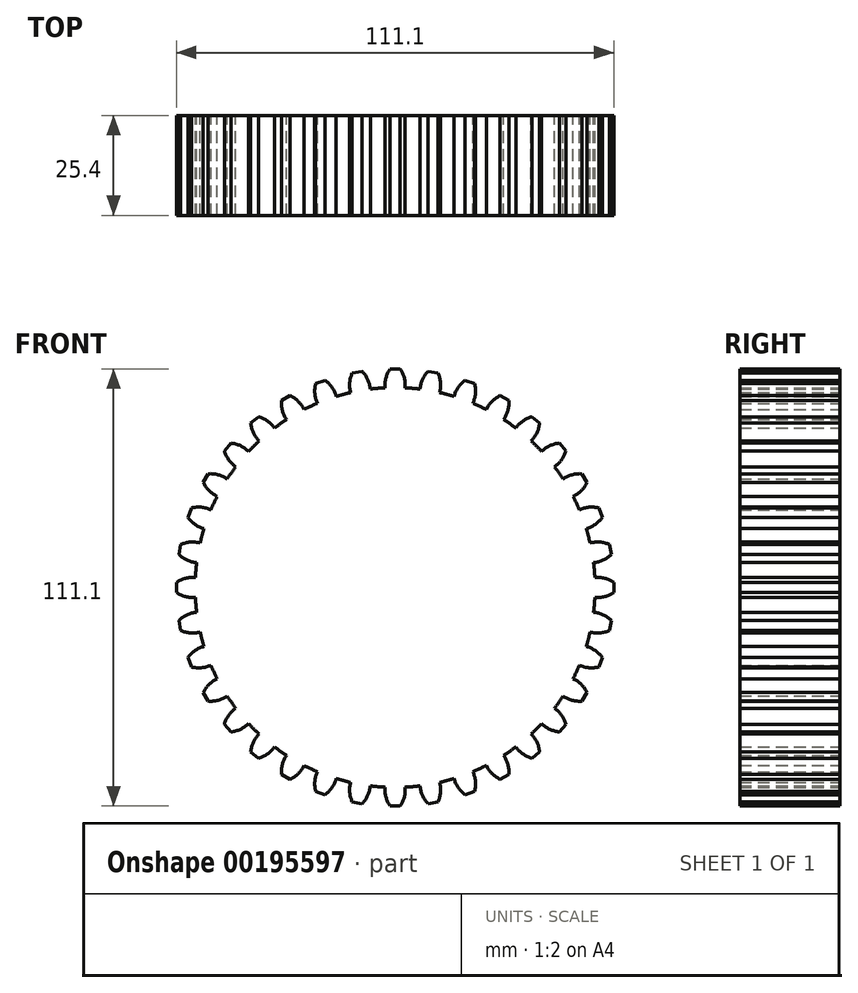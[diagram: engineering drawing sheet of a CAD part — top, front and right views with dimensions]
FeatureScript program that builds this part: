
annotation { "Feature Type Name" : "Feature", "Feature Type Description" : "" }
export const myFeature = defineFeature(function(context is Context, id is Id, definition is map)
    precondition{}
    {
        {
            var Q0;
            Q0=qCreatedBy(makeId("Front.planeOp"),FACE);
            var sketch = newSketch(context, id + "F0", { "sketchPlane" : qUnion([Q0])});
            skCircle(sketch, "E0", {"center": v(0, 0) * mm, "radius": 50.8 * mm});
            skPoint(sketch, "E1", {"position": v(0, 50.8) * mm});
            skPoint(sketch, "E2", {"position": v(0, 55.55) * mm});
            skPoint(sketch, "E3", {"position": v(-1.27, 55.55) * mm});
            skPoint(sketch, "E4", {"position": v(1.27, 55.55) * mm});
            skPoint(sketch, "E5", {"position": v(-2.54, 50.74) * mm});
            skPoint(sketch, "E6", {"position": v(2.54, 50.74) * mm});
            skArc(sketch, "E7", {"start": v(-1.27, 55.55) * mm, "mid": v(-2.32, 53.25) * mm, "end": v(-2.54, 50.74) * mm});
            skLineSegment(sketch, "E8", {"start": v(0, 55.55) * mm, "end": v(0, 50.8) * mm});
            skArc(sketch, "E9.MirrorCS", {"start": v(1.27, 55.55) * mm, "mid": v(2.32, 53.25) * mm, "end": v(2.54, 50.74) * mm});
            skLineSegment(sketch, "E10", {"start": v(-1.27, 55.55) * mm, "end": v(1.27, 55.55) * mm});
            skArc(sketch, "E11.1.0", {"start": v(-10.9, 54.49) * mm, "mid": v(-11.54, 52.04) * mm, "end": v(-11.31, 49.52) * mm});
            skLineSegment(sketch, "E11.1.1", {"start": v(-10.9, 54.49) * mm, "end": v(-8.4, 54.93) * mm});
            skArc(sketch, "E11.1.2", {"start": v(-8.4, 54.93) * mm, "mid": v(-6.96, 52.85) * mm, "end": v(-6.3, 50.4) * mm});
            skArc(sketch, "E11.2.0", {"start": v(-20.2, 51.77) * mm, "mid": v(-20.4, 49.25) * mm, "end": v(-19.74, 46.8) * mm});
            skLineSegment(sketch, "E11.2.1", {"start": v(-20.2, 51.77) * mm, "end": v(-17.8, 52.63) * mm});
            skArc(sketch, "E11.2.2", {"start": v(-17.8, 52.63) * mm, "mid": v(-16.03, 50.84) * mm, "end": v(-14.97, 48.55) * mm});
            skArc(sketch, "E11.3.0", {"start": v(-28.87, 47.47) * mm, "mid": v(-28.64, 44.96) * mm, "end": v(-27.57, 42.67) * mm});
            skLineSegment(sketch, "E11.3.1", {"start": v(-28.87, 47.47) * mm, "end": v(-26.68, 48.74) * mm});
            skArc(sketch, "E11.3.2", {"start": v(-26.68, 48.74) * mm, "mid": v(-24.61, 47.28) * mm, "end": v(-23.17, 45.2) * mm});
            skArc(sketch, "E11.4.0", {"start": v(-36.68, 41.74) * mm, "mid": v(-36.01, 39.3) * mm, "end": v(-34.56, 37.23) * mm});
            skLineSegment(sketch, "E11.4.1", {"start": v(-36.68, 41.74) * mm, "end": v(-34.73, 43.37) * mm});
            skArc(sketch, "E11.4.2", {"start": v(-34.73, 43.37) * mm, "mid": v(-32.45, 42.29) * mm, "end": v(-30.67, 40.5) * mm});
            skArc(sketch, "E11.5.0", {"start": v(-43.37, 34.73) * mm, "mid": v(-42.29, 32.45) * mm, "end": v(-40.5, 30.67) * mm});
            skLineSegment(sketch, "E11.5.1", {"start": v(-43.37, 34.73) * mm, "end": v(-41.74, 36.68) * mm});
            skArc(sketch, "E11.5.2", {"start": v(-41.74, 36.68) * mm, "mid": v(-39.3, 36.01) * mm, "end": v(-37.23, 34.56) * mm});
            skArc(sketch, "E11.6.0", {"start": v(-48.74, 26.68) * mm, "mid": v(-47.28, 24.61) * mm, "end": v(-45.2, 23.17) * mm});
            skLineSegment(sketch, "E11.6.1", {"start": v(-48.74, 26.68) * mm, "end": v(-47.47, 28.87) * mm});
            skArc(sketch, "E11.6.2", {"start": v(-47.47, 28.87) * mm, "mid": v(-44.96, 28.64) * mm, "end": v(-42.67, 27.57) * mm});
            skArc(sketch, "E11.7.0", {"start": v(-52.63, 17.8) * mm, "mid": v(-50.84, 16.03) * mm, "end": v(-48.55, 14.97) * mm});
            skLineSegment(sketch, "E11.7.1", {"start": v(-52.63, 17.8) * mm, "end": v(-51.77, 20.2) * mm});
            skArc(sketch, "E11.7.2", {"start": v(-51.77, 20.2) * mm, "mid": v(-49.25, 20.4) * mm, "end": v(-46.8, 19.74) * mm});
            skArc(sketch, "E11.8.0", {"start": v(-54.93, 8.4) * mm, "mid": v(-52.85, 6.96) * mm, "end": v(-50.4, 6.3) * mm});
            skLineSegment(sketch, "E11.8.1", {"start": v(-54.93, 8.4) * mm, "end": v(-54.49, 10.9) * mm});
            skArc(sketch, "E11.8.2", {"start": v(-54.49, 10.9) * mm, "mid": v(-52.04, 11.54) * mm, "end": v(-49.52, 11.31) * mm});
            skArc(sketch, "E11.9.0", {"start": v(-55.55, -1.27) * mm, "mid": v(-53.25, -2.32) * mm, "end": v(-50.74, -2.54) * mm});
            skLineSegment(sketch, "E11.9.1", {"start": v(-55.55, -1.27) * mm, "end": v(-55.55, 1.27) * mm});
            skArc(sketch, "E11.9.2", {"start": v(-55.55, 1.27) * mm, "mid": v(-53.25, 2.32) * mm, "end": v(-50.74, 2.54) * mm});
            skArc(sketch, "E11.10.0", {"start": v(-54.49, -10.9) * mm, "mid": v(-52.04, -11.54) * mm, "end": v(-49.52, -11.31) * mm});
            skLineSegment(sketch, "E11.10.1", {"start": v(-54.49, -10.9) * mm, "end": v(-54.93, -8.4) * mm});
            skArc(sketch, "E11.10.2", {"start": v(-54.93, -8.4) * mm, "mid": v(-52.85, -6.96) * mm, "end": v(-50.4, -6.3) * mm});
            skArc(sketch, "E11.11.0", {"start": v(-51.77, -20.2) * mm, "mid": v(-49.25, -20.4) * mm, "end": v(-46.8, -19.74) * mm});
            skLineSegment(sketch, "E11.11.1", {"start": v(-51.77, -20.2) * mm, "end": v(-52.63, -17.8) * mm});
            skArc(sketch, "E11.11.2", {"start": v(-52.63, -17.8) * mm, "mid": v(-50.84, -16.03) * mm, "end": v(-48.55, -14.97) * mm});
            skArc(sketch, "E11.12.0", {"start": v(-47.47, -28.87) * mm, "mid": v(-44.96, -28.64) * mm, "end": v(-42.67, -27.57) * mm});
            skLineSegment(sketch, "E11.12.1", {"start": v(-47.47, -28.87) * mm, "end": v(-48.74, -26.68) * mm});
            skArc(sketch, "E11.12.2", {"start": v(-48.74, -26.68) * mm, "mid": v(-47.28, -24.61) * mm, "end": v(-45.2, -23.17) * mm});
            skArc(sketch, "E11.13.0", {"start": v(-41.74, -36.68) * mm, "mid": v(-39.3, -36.01) * mm, "end": v(-37.23, -34.56) * mm});
            skLineSegment(sketch, "E11.13.1", {"start": v(-41.74, -36.68) * mm, "end": v(-43.37, -34.73) * mm});
            skArc(sketch, "E11.13.2", {"start": v(-43.37, -34.73) * mm, "mid": v(-42.29, -32.45) * mm, "end": v(-40.5, -30.67) * mm});
            skArc(sketch, "E11.14.0", {"start": v(-34.73, -43.37) * mm, "mid": v(-32.45, -42.29) * mm, "end": v(-30.67, -40.5) * mm});
            skLineSegment(sketch, "E11.14.1", {"start": v(-34.73, -43.37) * mm, "end": v(-36.68, -41.74) * mm});
            skArc(sketch, "E11.14.2", {"start": v(-36.68, -41.74) * mm, "mid": v(-36.01, -39.3) * mm, "end": v(-34.56, -37.23) * mm});
            skArc(sketch, "E11.15.0", {"start": v(-26.68, -48.74) * mm, "mid": v(-24.61, -47.28) * mm, "end": v(-23.17, -45.2) * mm});
            skLineSegment(sketch, "E11.15.1", {"start": v(-26.68, -48.74) * mm, "end": v(-28.87, -47.47) * mm});
            skArc(sketch, "E11.15.2", {"start": v(-28.87, -47.47) * mm, "mid": v(-28.64, -44.96) * mm, "end": v(-27.57, -42.67) * mm});
            skArc(sketch, "E11.16.0", {"start": v(-17.8, -52.63) * mm, "mid": v(-16.03, -50.84) * mm, "end": v(-14.97, -48.55) * mm});
            skLineSegment(sketch, "E11.16.1", {"start": v(-17.8, -52.63) * mm, "end": v(-20.2, -51.77) * mm});
            skArc(sketch, "E11.16.2", {"start": v(-20.2, -51.77) * mm, "mid": v(-20.4, -49.25) * mm, "end": v(-19.74, -46.8) * mm});
            skArc(sketch, "E11.17.0", {"start": v(-8.4, -54.93) * mm, "mid": v(-6.96, -52.85) * mm, "end": v(-6.3, -50.4) * mm});
            skLineSegment(sketch, "E11.17.1", {"start": v(-8.4, -54.93) * mm, "end": v(-10.9, -54.49) * mm});
            skArc(sketch, "E11.17.2", {"start": v(-10.9, -54.49) * mm, "mid": v(-11.54, -52.04) * mm, "end": v(-11.31, -49.52) * mm});
            skArc(sketch, "E11.18.0", {"start": v(1.27, -55.55) * mm, "mid": v(2.32, -53.25) * mm, "end": v(2.54, -50.74) * mm});
            skLineSegment(sketch, "E11.18.1", {"start": v(1.27, -55.55) * mm, "end": v(-1.27, -55.55) * mm});
            skArc(sketch, "E11.18.2", {"start": v(-1.27, -55.55) * mm, "mid": v(-2.32, -53.25) * mm, "end": v(-2.54, -50.74) * mm});
            skArc(sketch, "E11.19.0", {"start": v(10.9, -54.49) * mm, "mid": v(11.54, -52.04) * mm, "end": v(11.31, -49.52) * mm});
            skLineSegment(sketch, "E11.19.1", {"start": v(10.9, -54.49) * mm, "end": v(8.4, -54.93) * mm});
            skArc(sketch, "E11.19.2", {"start": v(8.4, -54.93) * mm, "mid": v(6.96, -52.85) * mm, "end": v(6.3, -50.4) * mm});
            skArc(sketch, "E11.20.0", {"start": v(20.2, -51.77) * mm, "mid": v(20.4, -49.25) * mm, "end": v(19.74, -46.8) * mm});
            skLineSegment(sketch, "E11.20.1", {"start": v(20.2, -51.77) * mm, "end": v(17.8, -52.63) * mm});
            skArc(sketch, "E11.20.2", {"start": v(17.8, -52.63) * mm, "mid": v(16.03, -50.84) * mm, "end": v(14.97, -48.55) * mm});
            skArc(sketch, "E11.21.0", {"start": v(28.87, -47.47) * mm, "mid": v(28.64, -44.96) * mm, "end": v(27.57, -42.67) * mm});
            skLineSegment(sketch, "E11.21.1", {"start": v(28.87, -47.47) * mm, "end": v(26.68, -48.74) * mm});
            skArc(sketch, "E11.21.2", {"start": v(26.68, -48.74) * mm, "mid": v(24.61, -47.28) * mm, "end": v(23.17, -45.2) * mm});
            skArc(sketch, "E11.22.0", {"start": v(36.68, -41.74) * mm, "mid": v(36.01, -39.3) * mm, "end": v(34.56, -37.23) * mm});
            skLineSegment(sketch, "E11.22.1", {"start": v(36.68, -41.74) * mm, "end": v(34.73, -43.37) * mm});
            skArc(sketch, "E11.22.2", {"start": v(34.73, -43.37) * mm, "mid": v(32.45, -42.29) * mm, "end": v(30.67, -40.5) * mm});
            skArc(sketch, "E11.23.0", {"start": v(43.37, -34.73) * mm, "mid": v(42.29, -32.45) * mm, "end": v(40.5, -30.67) * mm});
            skLineSegment(sketch, "E11.23.1", {"start": v(43.37, -34.73) * mm, "end": v(41.74, -36.68) * mm});
            skArc(sketch, "E11.23.2", {"start": v(41.74, -36.68) * mm, "mid": v(39.3, -36.01) * mm, "end": v(37.23, -34.56) * mm});
            skArc(sketch, "E11.24.0", {"start": v(48.74, -26.68) * mm, "mid": v(47.28, -24.61) * mm, "end": v(45.2, -23.17) * mm});
            skLineSegment(sketch, "E11.24.1", {"start": v(48.74, -26.68) * mm, "end": v(47.47, -28.87) * mm});
            skArc(sketch, "E11.24.2", {"start": v(47.47, -28.87) * mm, "mid": v(44.96, -28.64) * mm, "end": v(42.67, -27.57) * mm});
            skArc(sketch, "E11.25.0", {"start": v(52.63, -17.8) * mm, "mid": v(50.84, -16.03) * mm, "end": v(48.55, -14.97) * mm});
            skLineSegment(sketch, "E11.25.1", {"start": v(52.63, -17.8) * mm, "end": v(51.77, -20.2) * mm});
            skArc(sketch, "E11.25.2", {"start": v(51.77, -20.2) * mm, "mid": v(49.25, -20.4) * mm, "end": v(46.8, -19.74) * mm});
            skArc(sketch, "E11.26.0", {"start": v(54.93, -8.4) * mm, "mid": v(52.85, -6.96) * mm, "end": v(50.4, -6.3) * mm});
            skLineSegment(sketch, "E11.26.1", {"start": v(54.93, -8.4) * mm, "end": v(54.49, -10.9) * mm});
            skArc(sketch, "E11.26.2", {"start": v(54.49, -10.9) * mm, "mid": v(52.04, -11.54) * mm, "end": v(49.52, -11.31) * mm});
            skArc(sketch, "E11.27.0", {"start": v(55.55, 1.27) * mm, "mid": v(53.25, 2.32) * mm, "end": v(50.74, 2.54) * mm});
            skLineSegment(sketch, "E11.27.1", {"start": v(55.55, 1.27) * mm, "end": v(55.55, -1.27) * mm});
            skArc(sketch, "E11.27.2", {"start": v(55.55, -1.27) * mm, "mid": v(53.25, -2.32) * mm, "end": v(50.74, -2.54) * mm});
            skArc(sketch, "E11.28.0", {"start": v(54.49, 10.9) * mm, "mid": v(52.04, 11.54) * mm, "end": v(49.52, 11.31) * mm});
            skLineSegment(sketch, "E11.28.1", {"start": v(54.49, 10.9) * mm, "end": v(54.93, 8.4) * mm});
            skArc(sketch, "E11.28.2", {"start": v(54.93, 8.4) * mm, "mid": v(52.85, 6.96) * mm, "end": v(50.4, 6.3) * mm});
            skArc(sketch, "E11.29.0", {"start": v(51.77, 20.2) * mm, "mid": v(49.25, 20.4) * mm, "end": v(46.8, 19.74) * mm});
            skLineSegment(sketch, "E11.29.1", {"start": v(51.77, 20.2) * mm, "end": v(52.63, 17.8) * mm});
            skArc(sketch, "E11.29.2", {"start": v(52.63, 17.8) * mm, "mid": v(50.84, 16.03) * mm, "end": v(48.55, 14.97) * mm});
            skArc(sketch, "E11.30.0", {"start": v(47.47, 28.87) * mm, "mid": v(44.96, 28.64) * mm, "end": v(42.67, 27.57) * mm});
            skLineSegment(sketch, "E11.30.1", {"start": v(47.47, 28.87) * mm, "end": v(48.74, 26.68) * mm});
            skArc(sketch, "E11.30.2", {"start": v(48.74, 26.68) * mm, "mid": v(47.28, 24.61) * mm, "end": v(45.2, 23.17) * mm});
            skArc(sketch, "E11.31.0", {"start": v(41.74, 36.68) * mm, "mid": v(39.3, 36.01) * mm, "end": v(37.23, 34.56) * mm});
            skLineSegment(sketch, "E11.31.1", {"start": v(41.74, 36.68) * mm, "end": v(43.37, 34.73) * mm});
            skArc(sketch, "E11.31.2", {"start": v(43.37, 34.73) * mm, "mid": v(42.29, 32.45) * mm, "end": v(40.5, 30.67) * mm});
            skArc(sketch, "E11.32.0", {"start": v(34.73, 43.37) * mm, "mid": v(32.45, 42.29) * mm, "end": v(30.67, 40.5) * mm});
            skLineSegment(sketch, "E11.32.1", {"start": v(34.73, 43.37) * mm, "end": v(36.68, 41.74) * mm});
            skArc(sketch, "E11.32.2", {"start": v(36.68, 41.74) * mm, "mid": v(36.01, 39.3) * mm, "end": v(34.56, 37.23) * mm});
            skArc(sketch, "E11.33.0", {"start": v(26.68, 48.74) * mm, "mid": v(24.61, 47.28) * mm, "end": v(23.17, 45.2) * mm});
            skLineSegment(sketch, "E11.33.1", {"start": v(26.68, 48.74) * mm, "end": v(28.87, 47.47) * mm});
            skArc(sketch, "E11.33.2", {"start": v(28.87, 47.47) * mm, "mid": v(28.64, 44.96) * mm, "end": v(27.57, 42.67) * mm});
            skArc(sketch, "E11.34.0", {"start": v(17.8, 52.63) * mm, "mid": v(16.03, 50.84) * mm, "end": v(14.97, 48.55) * mm});
            skLineSegment(sketch, "E11.34.1", {"start": v(17.8, 52.63) * mm, "end": v(20.2, 51.77) * mm});
            skArc(sketch, "E11.34.2", {"start": v(20.2, 51.77) * mm, "mid": v(20.4, 49.25) * mm, "end": v(19.74, 46.8) * mm});
            skArc(sketch, "E11.35.0", {"start": v(8.4, 54.93) * mm, "mid": v(6.96, 52.85) * mm, "end": v(6.3, 50.4) * mm});
            skLineSegment(sketch, "E11.35.1", {"start": v(8.4, 54.93) * mm, "end": v(10.9, 54.49) * mm});
            skArc(sketch, "E11.35.2", {"start": v(10.9, 54.49) * mm, "mid": v(11.54, 52.04) * mm, "end": v(11.31, 49.52) * mm});
            skSolve(sketch);
        }
        {
            var Q0;
            {var subQ0=sQuery(id+"F0.wireOp",EDGE,"E0");var subQ35=makeQuery(id+"F0.imprint","INTERSECT",VERTEX,{"derivedFrom":[subQ0,sQuery(id+"F0.wireOp",EDGE,"E11.27.0")]});Q0=makeQuery(id+"F0.imprint","IMPRINT",FACE,{"disambiguationData":[TD([[makeQuery(id+"F0.imprint","IMPRINT",EDGE,{"disambiguationData":[TD([[subQ35,-1.0]])],"derivedFrom":subQ0}),1.0]])]});}
            var Q1;
            {var subQ0=sQuery(id+"F0.wireOp",EDGE,"E11.6.0");Q1=makeQuery(id+"F0.imprint","IMPRINT",FACE,{"disambiguationData":[TD([[makeQuery(id+"F0.imprint","IMPRINT",EDGE,{"derivedFrom":subQ0}),1.0]])]});}
            var Q2;
            {var subQ0=sQuery(id+"F0.wireOp",EDGE,"E11.7.0");Q2=makeQuery(id+"F0.imprint","IMPRINT",FACE,{"disambiguationData":[TD([[makeQuery(id+"F0.imprint","IMPRINT",EDGE,{"derivedFrom":subQ0}),1.0]])]});}
            var Q3;
            {var subQ0=sQuery(id+"F0.wireOp",EDGE,"E11.8.0");Q3=makeQuery(id+"F0.imprint","IMPRINT",FACE,{"disambiguationData":[TD([[makeQuery(id+"F0.imprint","IMPRINT",EDGE,{"derivedFrom":subQ0}),1.0]])]});}
            var Q4;
            {var subQ0=sQuery(id+"F0.wireOp",EDGE,"E11.9.0");Q4=makeQuery(id+"F0.imprint","IMPRINT",FACE,{"disambiguationData":[TD([[makeQuery(id+"F0.imprint","IMPRINT",EDGE,{"derivedFrom":subQ0}),1.0]])]});}
            var Q5;
            {var subQ0=sQuery(id+"F0.wireOp",EDGE,"E11.10.0");Q5=makeQuery(id+"F0.imprint","IMPRINT",FACE,{"disambiguationData":[TD([[makeQuery(id+"F0.imprint","IMPRINT",EDGE,{"derivedFrom":subQ0}),1.0]])]});}
            var Q6;
            {var subQ0=sQuery(id+"F0.wireOp",EDGE,"E11.11.0");Q6=makeQuery(id+"F0.imprint","IMPRINT",FACE,{"disambiguationData":[TD([[makeQuery(id+"F0.imprint","IMPRINT",EDGE,{"derivedFrom":subQ0}),1.0]])]});}
            var Q7;
            {var subQ0=sQuery(id+"F0.wireOp",EDGE,"E11.12.0");Q7=makeQuery(id+"F0.imprint","IMPRINT",FACE,{"disambiguationData":[TD([[makeQuery(id+"F0.imprint","IMPRINT",EDGE,{"derivedFrom":subQ0}),1.0]])]});}
            var Q8;
            {var subQ0=sQuery(id+"F0.wireOp",EDGE,"E11.13.0");Q8=makeQuery(id+"F0.imprint","IMPRINT",FACE,{"disambiguationData":[TD([[makeQuery(id+"F0.imprint","IMPRINT",EDGE,{"derivedFrom":subQ0}),1.0]])]});}
            var Q9;
            {var subQ0=sQuery(id+"F0.wireOp",EDGE,"E11.14.0");Q9=makeQuery(id+"F0.imprint","IMPRINT",FACE,{"disambiguationData":[TD([[makeQuery(id+"F0.imprint","IMPRINT",EDGE,{"derivedFrom":subQ0}),1.0]])]});}
            var Q10;
            {var subQ0=sQuery(id+"F0.wireOp",EDGE,"E11.15.0");Q10=makeQuery(id+"F0.imprint","IMPRINT",FACE,{"disambiguationData":[TD([[makeQuery(id+"F0.imprint","IMPRINT",EDGE,{"derivedFrom":subQ0}),1.0]])]});}
            var Q11;
            {var subQ0=sQuery(id+"F0.wireOp",EDGE,"E11.16.0");Q11=makeQuery(id+"F0.imprint","IMPRINT",FACE,{"disambiguationData":[TD([[makeQuery(id+"F0.imprint","IMPRINT",EDGE,{"derivedFrom":subQ0}),1.0]])]});}
            var Q12;
            {var subQ0=sQuery(id+"F0.wireOp",EDGE,"E11.17.0");Q12=makeQuery(id+"F0.imprint","IMPRINT",FACE,{"disambiguationData":[TD([[makeQuery(id+"F0.imprint","IMPRINT",EDGE,{"derivedFrom":subQ0}),1.0]])]});}
            var Q13;
            {var subQ0=sQuery(id+"F0.wireOp",EDGE,"E11.18.0");Q13=makeQuery(id+"F0.imprint","IMPRINT",FACE,{"disambiguationData":[TD([[makeQuery(id+"F0.imprint","IMPRINT",EDGE,{"derivedFrom":subQ0}),1.0]])]});}
            var Q14;
            {var subQ0=sQuery(id+"F0.wireOp",EDGE,"E11.19.0");Q14=makeQuery(id+"F0.imprint","IMPRINT",FACE,{"disambiguationData":[TD([[makeQuery(id+"F0.imprint","IMPRINT",EDGE,{"derivedFrom":subQ0}),1.0]])]});}
            var Q15;
            {var subQ0=sQuery(id+"F0.wireOp",EDGE,"E11.20.0");Q15=makeQuery(id+"F0.imprint","IMPRINT",FACE,{"disambiguationData":[TD([[makeQuery(id+"F0.imprint","IMPRINT",EDGE,{"derivedFrom":subQ0}),1.0]])]});}
            var Q16;
            {var subQ0=sQuery(id+"F0.wireOp",EDGE,"E11.21.0");Q16=makeQuery(id+"F0.imprint","IMPRINT",FACE,{"disambiguationData":[TD([[makeQuery(id+"F0.imprint","IMPRINT",EDGE,{"derivedFrom":subQ0}),1.0]])]});}
            var Q17;
            {var subQ0=sQuery(id+"F0.wireOp",EDGE,"E11.22.0");Q17=makeQuery(id+"F0.imprint","IMPRINT",FACE,{"disambiguationData":[TD([[makeQuery(id+"F0.imprint","IMPRINT",EDGE,{"derivedFrom":subQ0}),1.0]])]});}
            var Q18;
            {var subQ0=sQuery(id+"F0.wireOp",EDGE,"E11.23.0");Q18=makeQuery(id+"F0.imprint","IMPRINT",FACE,{"disambiguationData":[TD([[makeQuery(id+"F0.imprint","IMPRINT",EDGE,{"derivedFrom":subQ0}),1.0]])]});}
            var Q19;
            {var subQ0=sQuery(id+"F0.wireOp",EDGE,"E11.24.0");Q19=makeQuery(id+"F0.imprint","IMPRINT",FACE,{"disambiguationData":[TD([[makeQuery(id+"F0.imprint","IMPRINT",EDGE,{"derivedFrom":subQ0}),1.0]])]});}
            var Q20;
            {var subQ0=sQuery(id+"F0.wireOp",EDGE,"E11.25.0");Q20=makeQuery(id+"F0.imprint","IMPRINT",FACE,{"disambiguationData":[TD([[makeQuery(id+"F0.imprint","IMPRINT",EDGE,{"derivedFrom":subQ0}),1.0]])]});}
            var Q21;
            {var subQ0=sQuery(id+"F0.wireOp",EDGE,"E11.26.0");Q21=makeQuery(id+"F0.imprint","IMPRINT",FACE,{"disambiguationData":[TD([[makeQuery(id+"F0.imprint","IMPRINT",EDGE,{"derivedFrom":subQ0}),1.0]])]});}
            var Q22;
            {var subQ0=sQuery(id+"F0.wireOp",EDGE,"E11.27.0");Q22=makeQuery(id+"F0.imprint","IMPRINT",FACE,{"disambiguationData":[TD([[makeQuery(id+"F0.imprint","IMPRINT",EDGE,{"derivedFrom":subQ0}),1.0]])]});}
            var Q23;
            {var subQ0=sQuery(id+"F0.wireOp",EDGE,"E11.28.0");Q23=makeQuery(id+"F0.imprint","IMPRINT",FACE,{"disambiguationData":[TD([[makeQuery(id+"F0.imprint","IMPRINT",EDGE,{"derivedFrom":subQ0}),1.0]])]});}
            var Q24;
            {var subQ0=sQuery(id+"F0.wireOp",EDGE,"E11.29.0");Q24=makeQuery(id+"F0.imprint","IMPRINT",FACE,{"disambiguationData":[TD([[makeQuery(id+"F0.imprint","IMPRINT",EDGE,{"derivedFrom":subQ0}),1.0]])]});}
            var Q25;
            {var subQ0=sQuery(id+"F0.wireOp",EDGE,"E11.30.0");Q25=makeQuery(id+"F0.imprint","IMPRINT",FACE,{"disambiguationData":[TD([[makeQuery(id+"F0.imprint","IMPRINT",EDGE,{"derivedFrom":subQ0}),1.0]])]});}
            var Q26;
            {var subQ0=sQuery(id+"F0.wireOp",EDGE,"E11.31.0");Q26=makeQuery(id+"F0.imprint","IMPRINT",FACE,{"disambiguationData":[TD([[makeQuery(id+"F0.imprint","IMPRINT",EDGE,{"derivedFrom":subQ0}),1.0]])]});}
            var Q27;
            {var subQ0=sQuery(id+"F0.wireOp",EDGE,"E11.32.0");Q27=makeQuery(id+"F0.imprint","IMPRINT",FACE,{"disambiguationData":[TD([[makeQuery(id+"F0.imprint","IMPRINT",EDGE,{"derivedFrom":subQ0}),1.0]])]});}
            var Q28;
            {var subQ0=sQuery(id+"F0.wireOp",EDGE,"E11.33.0");Q28=makeQuery(id+"F0.imprint","IMPRINT",FACE,{"disambiguationData":[TD([[makeQuery(id+"F0.imprint","IMPRINT",EDGE,{"derivedFrom":subQ0}),1.0]])]});}
            var Q29;
            {var subQ0=sQuery(id+"F0.wireOp",EDGE,"E11.34.0");Q29=makeQuery(id+"F0.imprint","IMPRINT",FACE,{"disambiguationData":[TD([[makeQuery(id+"F0.imprint","IMPRINT",EDGE,{"derivedFrom":subQ0}),1.0]])]});}
            var Q30;
            {var subQ0=sQuery(id+"F0.wireOp",EDGE,"E11.35.0");Q30=makeQuery(id+"F0.imprint","IMPRINT",FACE,{"disambiguationData":[TD([[makeQuery(id+"F0.imprint","IMPRINT",EDGE,{"derivedFrom":subQ0}),1.0]])]});}
            var Q31;
            {var subQ0=sQuery(id+"F0.wireOp",EDGE,"E7");Q31=makeQuery(id+"F0.imprint","IMPRINT",FACE,{"disambiguationData":[TD([[makeQuery(id+"F0.imprint","IMPRINT",EDGE,{"derivedFrom":subQ0}),1.0]])]});}
            var Q32;
            {var subQ0=sQuery(id+"F0.wireOp",EDGE,"E11.5.0");Q32=makeQuery(id+"F0.imprint","IMPRINT",FACE,{"disambiguationData":[TD([[makeQuery(id+"F0.imprint","IMPRINT",EDGE,{"derivedFrom":subQ0}),1.0]])]});}
            var Q33;
            {var subQ0=sQuery(id+"F0.wireOp",EDGE,"E11.4.0");Q33=makeQuery(id+"F0.imprint","IMPRINT",FACE,{"disambiguationData":[TD([[makeQuery(id+"F0.imprint","IMPRINT",EDGE,{"derivedFrom":subQ0}),1.0]])]});}
            var Q34;
            {var subQ0=sQuery(id+"F0.wireOp",EDGE,"E11.3.0");Q34=makeQuery(id+"F0.imprint","IMPRINT",FACE,{"disambiguationData":[TD([[makeQuery(id+"F0.imprint","IMPRINT",EDGE,{"derivedFrom":subQ0}),1.0]])]});}
            var Q35;
            {var subQ0=sQuery(id+"F0.wireOp",EDGE,"E11.2.0");Q35=makeQuery(id+"F0.imprint","IMPRINT",FACE,{"disambiguationData":[TD([[makeQuery(id+"F0.imprint","IMPRINT",EDGE,{"derivedFrom":subQ0}),1.0]])]});}
            var Q36;
            {var subQ0=sQuery(id+"F0.wireOp",EDGE,"E11.1.0");Q36=makeQuery(id+"F0.imprint","IMPRINT",FACE,{"disambiguationData":[TD([[makeQuery(id+"F0.imprint","IMPRINT",EDGE,{"derivedFrom":subQ0}),1.0]])]});}
            var Q37;
            {var subQ0=sQuery(id+"F0.wireOp",EDGE,"E8");Q37=makeQuery(id+"F0.imprint","IMPRINT",FACE,{"disambiguationData":[TD([[makeQuery(id+"F0.imprint","IMPRINT",EDGE,{"derivedFrom":subQ0}),1.0]])]});}
            extrude(context, id + "F1", {"entities" : qUnion([Q0, Q1, Q2, Q3, Q4, Q5, Q6, Q7, Q8, Q9, Q10, Q11, Q12, Q13, Q14, Q15, Q16, Q17, Q18, Q19, Q20, Q21, Q22, Q23, Q24, Q25, Q26, Q27, Q28, Q29, Q30, Q31, Q32, Q33, Q34, Q35, Q36, Q37]), "depth" : 25.4 * mm});
        }
    });
